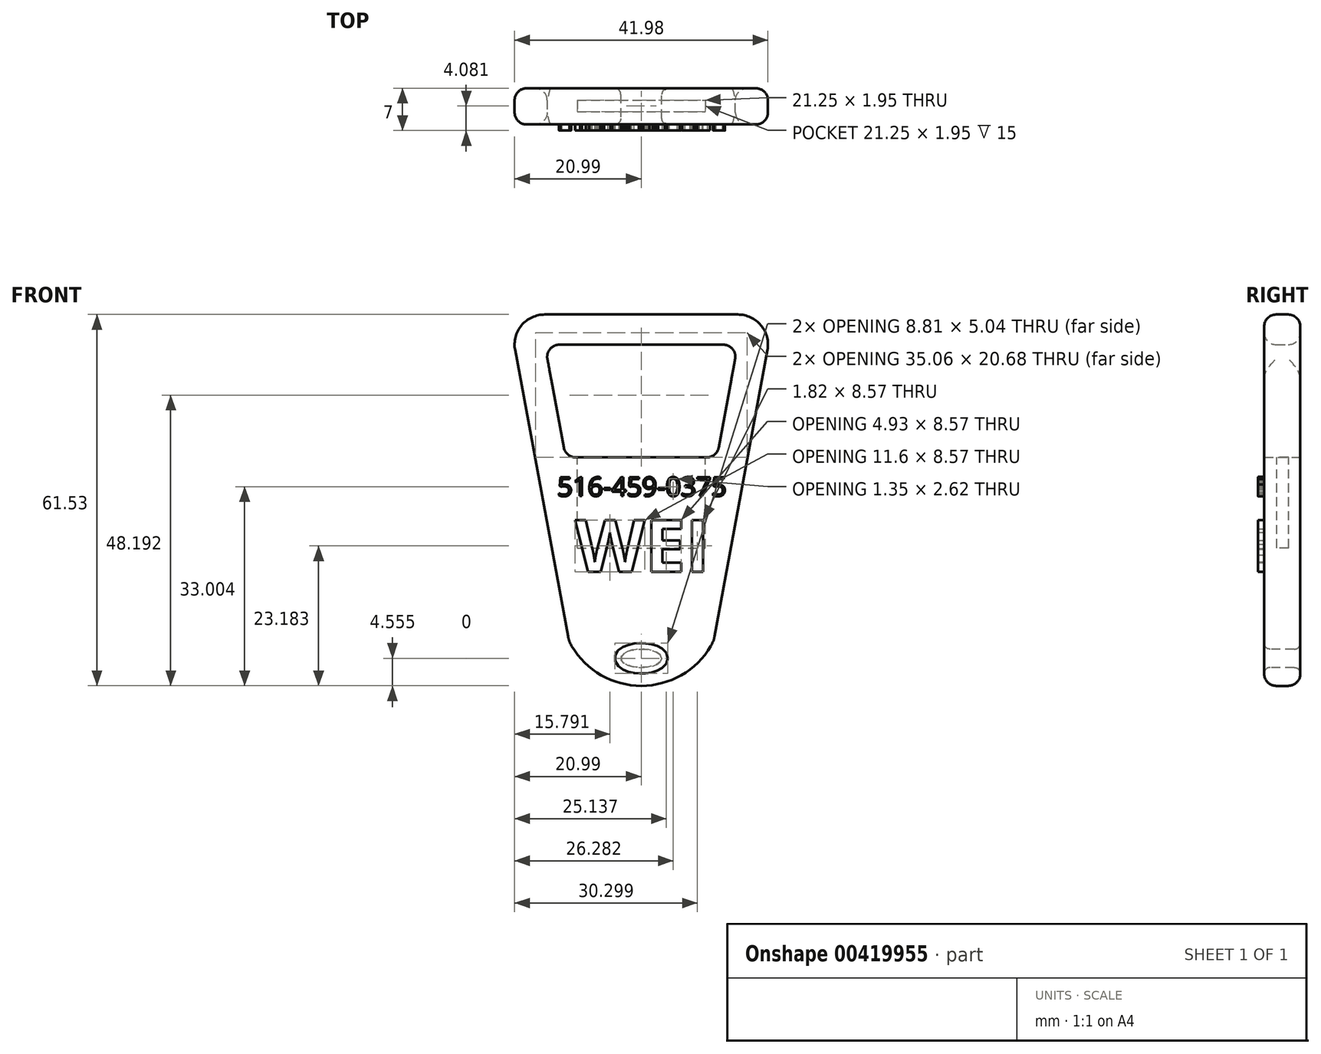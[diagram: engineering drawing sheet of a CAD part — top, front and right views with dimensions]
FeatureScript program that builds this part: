
annotation { "Feature Type Name" : "Feature", "Feature Type Description" : "" }
export const myFeature = defineFeature(function(context is Context, id is Id, definition is map)
    precondition{}
    {
        {
            var Q0;
            Q0=qCreatedBy(makeId("Front.planeOp"),FACE);
            var sketch = newSketch(context, id + "F0", { "sketchPlane" : qUnion([Q0])});
            skLineSegment(sketch, "E0", {"start": v(0, 24.3) * mm, "end": v(0, -29.14) * mm, "construction": true});
            skLineSegment(sketch, "E1", {"start": v(0, 23.68) * mm, "end": v(22, 23.68) * mm});
            skLineSegment(sketch, "E2", {"start": v(22, 23.68) * mm, "end": v(12, -30.4) * mm});
            skLineSegment(sketch, "E3", {"start": v(12, -30.4) * mm, "end": v(0, -30.4) * mm});
            skLineSegment(sketch, "E4.MirrorCS", {"start": v(0, 23.68) * mm, "end": v(-22, 23.68) * mm});
            skLineSegment(sketch, "E5.MirrorCS", {"start": v(-22, 23.68) * mm, "end": v(-12, -30.4) * mm});
            skLineSegment(sketch, "E6.MirrorCS", {"start": v(-12, -30.4) * mm, "end": v(0, -30.4) * mm});
            skLineSegment(sketch, "E7.0", {"start": v(-16, 18.68) * mm, "end": v(-12.54, 0) * mm});
            skLineSegment(sketch, "E7.1", {"start": v(-4.55, 18.68) * mm, "end": v(-16, 18.68) * mm});
            skLineSegment(sketch, "E7.2", {"start": v(-4.55, 18.68) * mm, "end": v(16, 18.68) * mm});
            skLineSegment(sketch, "E7.3", {"start": v(16, 18.68) * mm, "end": v(12.54, 0) * mm});
            skLineSegment(sketch, "E8", {"start": v(-12.54, 0) * mm, "end": v(12.54, 0) * mm});
            skArc(sketch, "E9", {"start": v(-12, -30.4) * mm, "mid": v(0, -37.85) * mm, "end": v(12, -30.4) * mm});
            skEllipse(sketch, "E10", {"center": v(0, -33.3) * mm, "majorRadius": 3.4 * mm, "minorRadius": 1.52 * mm, "majorAxis": v(1, 0)});
            skSolve(sketch);
        }
        {
            var Q0;
            Q0 = qSketchRegion(id + "F0", true);
            extrude(context, id + "F1", {"entities" : qUnion([Q0]), "depth" : 6 * mm});
        }
        {
            var Q0;
            Q0=makeQuery(id+"F1.opExtrude","SWEPT_EDGE",EDGE,{"disambiguationData":[OSD([sQuery(id+"F0.wireOp",EDGE,"E4.MirrorCS"),sQuery(id+"F0.wireOp",EDGE,"E5.MirrorCS")])]});
            var Q1;
            Q1=makeQuery(id+"F1.opExtrude","SWEPT_EDGE",EDGE,{"disambiguationData":[OSD([sQuery(id+"F0.wireOp",EDGE,"E1"),sQuery(id+"F0.wireOp",EDGE,"E2")])]});
            var Q2;
            Q2=makeQuery(id+"F1.opExtrude","SWEPT_EDGE",EDGE,{"disambiguationData":[OSD([sQuery(id+"F0.wireOp",EDGE,"E5.MirrorCS"),sQuery(id+"F0.wireOp",EDGE,"E6.MirrorCS")])]});
            var Q3;
            Q3=makeQuery(id+"F1.opExtrude","SWEPT_EDGE",EDGE,{"disambiguationData":[OSD([sQuery(id+"F0.wireOp",EDGE,"E2"),sQuery(id+"F0.wireOp",EDGE,"E3")])]});
            fillet(context, id + "F2", {"entities" : qUnion([Q0, Q1, Q2, Q3]), "radius" : 5 * mm, "tangentPropagation" : true, "allowEdgeOverflow" : false});
        }
        {
            var Q0;
            Q0=makeQuery(id+"F1.opExtrude","SWEPT_FACE",FACE,{"disambiguationData":[OSD([sQuery(id+"F0.wireOp",EDGE,"E8")])]});
            var sketch = newSketch(context, id + "F3", { "sketchPlane" : qUnion([Q0])});
            skLineSegment(sketch, "E11", {"start": v(0, -1.94) * mm, "end": v(10.62, -1.94) * mm});
            skLineSegment(sketch, "E12", {"start": v(10.62, -1.94) * mm, "end": v(10.62, -3.9) * mm});
            skLineSegment(sketch, "E13", {"start": v(10.62, -3.9) * mm, "end": v(0, -3.9) * mm});
            skLineSegment(sketch, "E14", {"start": v(0, -1.39) * mm, "end": v(0, -4.64) * mm, "construction": true});
            skLineSegment(sketch, "E15.MirrorCS", {"start": v(0, -1.94) * mm, "end": v(-10.62, -1.94) * mm});
            skLineSegment(sketch, "E16.MirrorCS", {"start": v(-10.62, -3.9) * mm, "end": v(0, -3.9) * mm});
            skLineSegment(sketch, "E17.MirrorCS", {"start": v(-10.62, -1.94) * mm, "end": v(-10.62, -3.9) * mm});
            skSolve(sketch);
        }
        {
            var Q0;
            Q0=makeQuery(id+"F1.opExtrude","CAP_EDGE",EDGE,{"disambiguationData":[OSD([sQuery(id+"F0.wireOp",EDGE,"E1"),sQuery(id+"F0.wireOp",EDGE,"E4.MirrorCS")])],"isStart":false});
            var Q1;
            Q1=makeQuery(id+"F1.opExtrude","SWEPT_FACE",FACE,{"disambiguationData":[OSD([sQuery(id+"F0.wireOp",EDGE,"E5.MirrorCS")])]});
            var Q2;
            Q2=makeQuery(id+"F1.opExtrude","SWEPT_EDGE",EDGE,{"disambiguationData":[OSD([sQuery(id+"F0.wireOp",EDGE,"E7.0"),sQuery(id+"F0.wireOp",EDGE,"E8")])]});
            var Q3;
            Q3=makeQuery(id+"F1.opExtrude","SWEPT_EDGE",EDGE,{"disambiguationData":[OSD([sQuery(id+"F0.wireOp",EDGE,"E7.3"),sQuery(id+"F0.wireOp",EDGE,"E8")])]});
            var Q4;
            Q4=makeQuery(id+"F1.opExtrude","SWEPT_EDGE",EDGE,{"disambiguationData":[OSD([sQuery(id+"F0.wireOp",EDGE,"E7.0"),sQuery(id+"F0.wireOp",EDGE,"E7.1")])]});
            var Q5;
            Q5=makeQuery(id+"F1.opExtrude","SWEPT_FACE",FACE,{"disambiguationData":[OSD([sQuery(id+"F0.wireOp",EDGE,"E7.1"),sQuery(id+"F0.wireOp",EDGE,"E7.2")])]});
            fillet(context, id + "F4", {"entities" : qUnion([Q0, Q1, Q2, Q3, Q4, Q5]), "radius" : 2 * mm, "tangentPropagation" : true, "allowEdgeOverflow" : false});
        }
        {
            var Q0;
            Q0 = qSketchRegion(id + "F3", true);
            extrude(context, id + "F5", {"entities" : qUnion([Q0]), "operationType" : NewBodyOperationType.REMOVE, "oppositeDirection" : true, "depth" : 15 * mm});
        }
        {
            var Q0;
            Q0=makeQuery(id+"F1.opExtrude","CAP_EDGE",EDGE,{"disambiguationData":[OSD([sQuery(id+"F0.wireOp",EDGE,"E10")])],"isStart":false});
            var Q1;
            Q1=makeQuery(id+"F1.opExtrude","CAP_EDGE",EDGE,{"disambiguationData":[OSD([sQuery(id+"F0.wireOp",EDGE,"E10")])],"isStart":true});
            fillet(context, id + "F6", {"entities" : qUnion([Q0, Q1]), "radius" : 1 * mm, "tangentPropagation" : true, "allowEdgeOverflow" : false});
        }
        {
            var Q0;
            Q0=makeQuery(id+"F1.opExtrude","CAP_FACE",FACE,{"disambiguationData":[OSD([sQuery(id+"F0.wireOp",EDGE,"E1"),sQuery(id+"F0.wireOp",EDGE,"E2"),sQuery(id+"F0.wireOp",EDGE,"E4.MirrorCS"),sQuery(id+"F0.wireOp",EDGE,"E5.MirrorCS"),sQuery(id+"F0.wireOp",EDGE,"E7.0"),sQuery(id+"F0.wireOp",EDGE,"E7.1"),sQuery(id+"F0.wireOp",EDGE,"E7.2"),sQuery(id+"F0.wireOp",EDGE,"E7.3"),sQuery(id+"F0.wireOp",EDGE,"E8"),sQuery(id+"F0.wireOp",EDGE,"E9"),sQuery(id+"F0.wireOp",EDGE,"E10")])],"isStart":false});
            var sketch = newSketch(context, id + "F7", { "sketchPlane" : qUnion([Q0])});
            skText(sketch, "E18", { "text": "WEI", "fontName": "OpenSans-Bold.ttf"});
            const initialGuessF7  = {"E18": [-0.011, -0.01895, 1, 0, 0.00864]};
            skSetInitialGuess(sketch, initialGuessF7);
            skSolve(sketch);
        }
        {
            var Q0;
            Q0 = qSketchRegion(id + "F7", true);
            extrude(context, id + "F8", {"entities" : qUnion([Q0]), "operationType" : NewBodyOperationType.ADD, "depth" : 1 * mm});
        }
        {
            var Q0;
            Q0=makeQuery(id+"F1.opExtrude","CAP_FACE",FACE,{"disambiguationData":[OSD([sQuery(id+"F0.wireOp",EDGE,"E1"),sQuery(id+"F0.wireOp",EDGE,"E2"),sQuery(id+"F0.wireOp",EDGE,"E4.MirrorCS"),sQuery(id+"F0.wireOp",EDGE,"E5.MirrorCS"),sQuery(id+"F0.wireOp",EDGE,"E7.0"),sQuery(id+"F0.wireOp",EDGE,"E7.1"),sQuery(id+"F0.wireOp",EDGE,"E7.2"),sQuery(id+"F0.wireOp",EDGE,"E7.3"),sQuery(id+"F0.wireOp",EDGE,"E8"),sQuery(id+"F0.wireOp",EDGE,"E9"),sQuery(id+"F0.wireOp",EDGE,"E10")])],"isStart":false});
            var sketch = newSketch(context, id + "F9", { "sketchPlane" : qUnion([Q0])});
            skText(sketch, "E19", { "text": "516-459-0375", "fontName": "OpenSans-Regular.ttf"});
            const initialGuessF9  = {"E19": [-0.0139, -0.00642, 1, 0, 0.00317]};
            skSetInitialGuess(sketch, initialGuessF9);
            skSolve(sketch);
        }
        {
            var Q0;
            Q0 = qSketchRegion(id + "F9", true);
            extrude(context, id + "F10", {"entities" : qUnion([Q0]), "depth" : 1 * mm});
        }
        {
            var Q0;
            Q0=makeQuery(id+"F1.opExtrude","SWEPT_BODY",BODY,{"disambiguationData":[OSD([sQuery(id+"F0.wireOp",EDGE,"E1"),sQuery(id+"F0.wireOp",EDGE,"E2"),sQuery(id+"F0.wireOp",EDGE,"E4.MirrorCS"),sQuery(id+"F0.wireOp",EDGE,"E5.MirrorCS"),sQuery(id+"F0.wireOp",EDGE,"E7.0"),sQuery(id+"F0.wireOp",EDGE,"E7.1"),sQuery(id+"F0.wireOp",EDGE,"E7.2"),sQuery(id+"F0.wireOp",EDGE,"E7.3"),sQuery(id+"F0.wireOp",EDGE,"E8"),sQuery(id+"F0.wireOp",EDGE,"E9"),sQuery(id+"F0.wireOp",EDGE,"E10")])]});
            transform(context, id + "F11", {"entities" : qUnion([Q0]), "transformType" : TransformType.TRANSLATION_3D, "dx" : 0 * mm, "dy" : 0 * mm, "dz" : 0 * mm, "makeCopy" : true});
        }
    });
